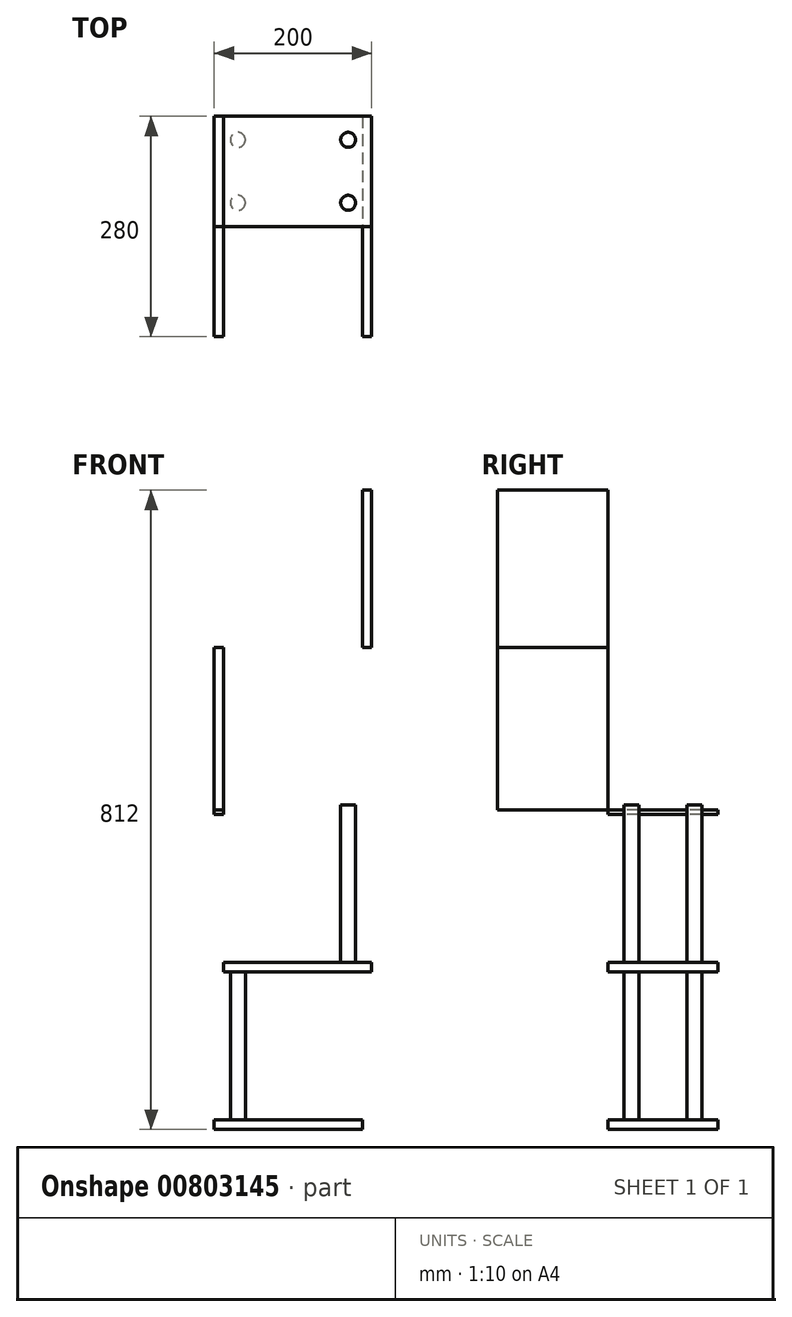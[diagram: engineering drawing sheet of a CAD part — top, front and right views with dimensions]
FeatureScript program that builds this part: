
annotation { "Feature Type Name" : "Feature", "Feature Type Description" : "" }
export const myFeature = defineFeature(function(context is Context, id is Id, definition is map)
    precondition{}
    {
        {
            var Q0;
            Q0=qCreatedBy(makeId("Front.planeOp"),FACE);
            var sketch = newSketch(context, id + "F0", { "sketchPlane" : qUnion([Q0])});
            skLineSegment(sketch, "E0.bottom", {"start": v(0, 0) * mm, "end": v(200, 0) * mm});
            skLineSegment(sketch, "E0.top", {"start": v(0, 12) * mm, "end": v(200, 12) * mm});
            skLineSegment(sketch, "E0.left", {"start": v(0, 0) * mm, "end": v(0, 12) * mm});
            skLineSegment(sketch, "E0.right", {"start": v(200, 0) * mm, "end": v(200, 12) * mm});
            skPoint(sketch, "E1.oppositeSnap0", {"position": v(0, 6) * mm});
            skLineSegment(sketch, "E1.bottom", {"start": v(0, 0) * mm, "end": v(12, 0) * mm});
            skLineSegment(sketch, "E1.top", {"start": v(0, 6) * mm, "end": v(12, 6) * mm});
            skLineSegment(sketch, "E1.left", {"start": v(0, 0) * mm, "end": v(0, 6) * mm});
            skLineSegment(sketch, "E1.right", {"start": v(12, 0) * mm, "end": v(12, 6) * mm});
            skSolve(sketch);
        }
        {
            var Q0;
            Q0=makeQuery(id+"F0.imprint","IMPRINT",FACE,{"disambiguationData":[TD([[makeQuery(id+"F0.imprint","IMPRINT",EDGE,{"derivedFrom":sQuery(id+"F0.wireOp",EDGE,"E0.bottom")}),1.0]])]});
            extrude(context, id + "F1", {"entities" : qUnion([Q0]), "oppositeDirection" : true, "depth" : 140 * mm, "offsetDistance" : 25 * mm});
        }
        {
            var Q0;
            Q0=makeQuery(id+"F1.opExtrude","SWEPT_FACE",FACE,{"disambiguationData":[OSD([sQuery(id+"F0.wireOp",EDGE,"E1.top")])]});
            var sketch = newSketch(context, id + "F2", { "sketchPlane" : qUnion([Q0])});
            skLineSegment(sketch, "E2.bottom", {"start": v(0, 0) * mm, "end": v(12, 0) * mm});
            skLineSegment(sketch, "E2.top", {"start": v(0, -140) * mm, "end": v(12, -140) * mm});
            skLineSegment(sketch, "E2.left", {"start": v(0, 0) * mm, "end": v(0, -140) * mm});
            skLineSegment(sketch, "E2.right", {"start": v(12, 0) * mm, "end": v(12, -140) * mm});
            skSolve(sketch);
        }
        {
            var Q0;
            Q0 = qSketchRegion(id + "F2", true);
            extrude(context, id + "F3", {"entities" : qUnion([Q0]), "operationType" : NewBodyOperationType.ADD, "depth" : 206 * mm, "offsetDistance" : 25 * mm});
        }
        {
            var Q0;
            Q0=makeQuery(id+"F3.opExtrude","SWEPT_FACE",FACE,{"disambiguationData":[OSD([sQuery(id+"F2.wireOp",EDGE,"E2.right")])]});
            var sketch = newSketch(context, id + "F4", { "sketchPlane" : qUnion([Q0])});
            skLineSegment(sketch, "E3.bottom", {"start": v(0, -200) * mm, "end": v(140, -200) * mm});
            skLineSegment(sketch, "E3.top", {"start": v(0, -188) * mm, "end": v(140, -188) * mm});
            skLineSegment(sketch, "E3.left", {"start": v(0, -200) * mm, "end": v(0, -188) * mm});
            skLineSegment(sketch, "E3.right", {"start": v(140, -200) * mm, "end": v(140, -188) * mm});
            skSolve(sketch);
        }
        {
            var Q0;
            Q0 = qSketchRegion(id + "F4", true);
            extrude(context, id + "F5", {"entities" : qUnion([Q0]), "operationType" : NewBodyOperationType.ADD, "depth" : 188 * mm, "offsetDistance" : 25 * mm});
        }
        {
            var Q0;
            Q0=makeQuery(id+"F5.boolean.opBoolean","MERGE",FACE,{"derivedFrom":[makeQuery(id+"F3.opExtrude","CAP_FACE",FACE,{"disambiguationData":[OSD([sQuery(id+"F2.wireOp",EDGE,"E2.bottom"),sQuery(id+"F2.wireOp",EDGE,"E2.top"),sQuery(id+"F2.wireOp",EDGE,"E2.left"),sQuery(id+"F2.wireOp",EDGE,"E2.right")])],"isStart":false}),makeQuery(id+"F5.opExtrude","SWEPT_FACE",FACE,{"disambiguationData":[OSD([sQuery(id+"F4.wireOp",EDGE,"E3.bottom")])]})]});
            var sketch = newSketch(context, id + "F6", { "sketchPlane" : qUnion([Q0])});
            skLineSegment(sketch, "E4.bottom", {"start": v(200, -140) * mm, "end": v(188, -140) * mm});
            skLineSegment(sketch, "E4.top", {"start": v(200, 0) * mm, "end": v(188, 0) * mm});
            skLineSegment(sketch, "E4.left", {"start": v(200, -140) * mm, "end": v(200, 0) * mm});
            skLineSegment(sketch, "E4.right", {"start": v(188, -140) * mm, "end": v(188, 0) * mm});
            skSolve(sketch);
        }
        {
            var Q0;
            Q0 = qSketchRegion(id + "F6", true);
            extrude(context, id + "F7", {"entities" : qUnion([Q0]), "operationType" : NewBodyOperationType.ADD, "depth" : 200 * mm, "offsetDistance" : 25 * mm});
        }
        {
            var Q0;
            Q0=makeQuery(id+"F7.opExtrude","SWEPT_FACE",FACE,{"disambiguationData":[OSD([sQuery(id+"F6.wireOp",EDGE,"E4.right")])]});
            var sketch = newSketch(context, id + "F8", { "sketchPlane" : qUnion([Q0])});
            skLineSegment(sketch, "E5.bottom", {"start": v(-140, -400) * mm, "end": v(0, -400) * mm});
            skLineSegment(sketch, "E5.top", {"start": v(-140, -388) * mm, "end": v(0, -388) * mm});
            skLineSegment(sketch, "E5.left", {"start": v(-140, -400) * mm, "end": v(-140, -388) * mm});
            skLineSegment(sketch, "E5.right", {"start": v(0, -400) * mm, "end": v(0, -388) * mm});
            skSolve(sketch);
        }
        {
            var Q0;
            Q0 = qSketchRegion(id + "F8", true);
            extrude(context, id + "F9", {"entities" : qUnion([Q0]), "operationType" : NewBodyOperationType.ADD, "depth" : 188 * mm, "offsetDistance" : 25 * mm});
        }
        {
            var Q0;
            Q0=makeQuery(id+"F9.opExtrude","SWEPT_FACE",FACE,{"disambiguationData":[OSD([sQuery(id+"F8.wireOp",EDGE,"E5.top")])]});
            var sketch = newSketch(context, id + "F10", { "sketchPlane" : qUnion([Q0])});
            skCircle(sketch, "E6", {"center": v(30, 30) * mm, "radius": 9.5 * mm});
            skCircle(sketch, "E7", {"center": v(30, 110) * mm, "radius": 9.5 * mm});
            skSolve(sketch);
        }
        {
            var Q0;
            Q0 = qSketchRegion(id + "F10", true);
            extrude(context, id + "F11", {"entities" : qUnion([Q0]), "operationType" : NewBodyOperationType.ADD, "depth" : 200 * mm, "offsetDistance" : 25 * mm});
        }
        {
            var Q0;
            Q0=makeQuery(id+"F5.opExtrude","SWEPT_FACE",FACE,{"disambiguationData":[OSD([sQuery(id+"F4.wireOp",EDGE,"E3.top")])]});
            var sketch = newSketch(context, id + "F12", { "sketchPlane" : qUnion([Q0])});
            skLineSegment(sketch, "E8", {"start": v(170, 140) * mm, "end": v(170, 110) * mm});
            skLineSegment(sketch, "E9", {"start": v(170, 110) * mm, "end": v(200, 110) * mm});
            skLineSegment(sketch, "E10", {"start": v(200, 30) * mm, "end": v(170, 30) * mm});
            skLineSegment(sketch, "E11", {"start": v(170, 30) * mm, "end": v(170, 0) * mm});
            skCircle(sketch, "E12", {"center": v(170, 30) * mm, "radius": 9.5 * mm});
            skCircle(sketch, "E13", {"center": v(170, 110) * mm, "radius": 9.5 * mm});
            skSolve(sketch);
        }
        {
            var Q0;
            Q0 = qSketchRegion(id + "F12", true);
            extrude(context, id + "F13", {"entities" : qUnion([Q0]), "operationType" : NewBodyOperationType.ADD, "depth" : 200 * mm, "offsetDistance" : 25 * mm});
        }
    });
